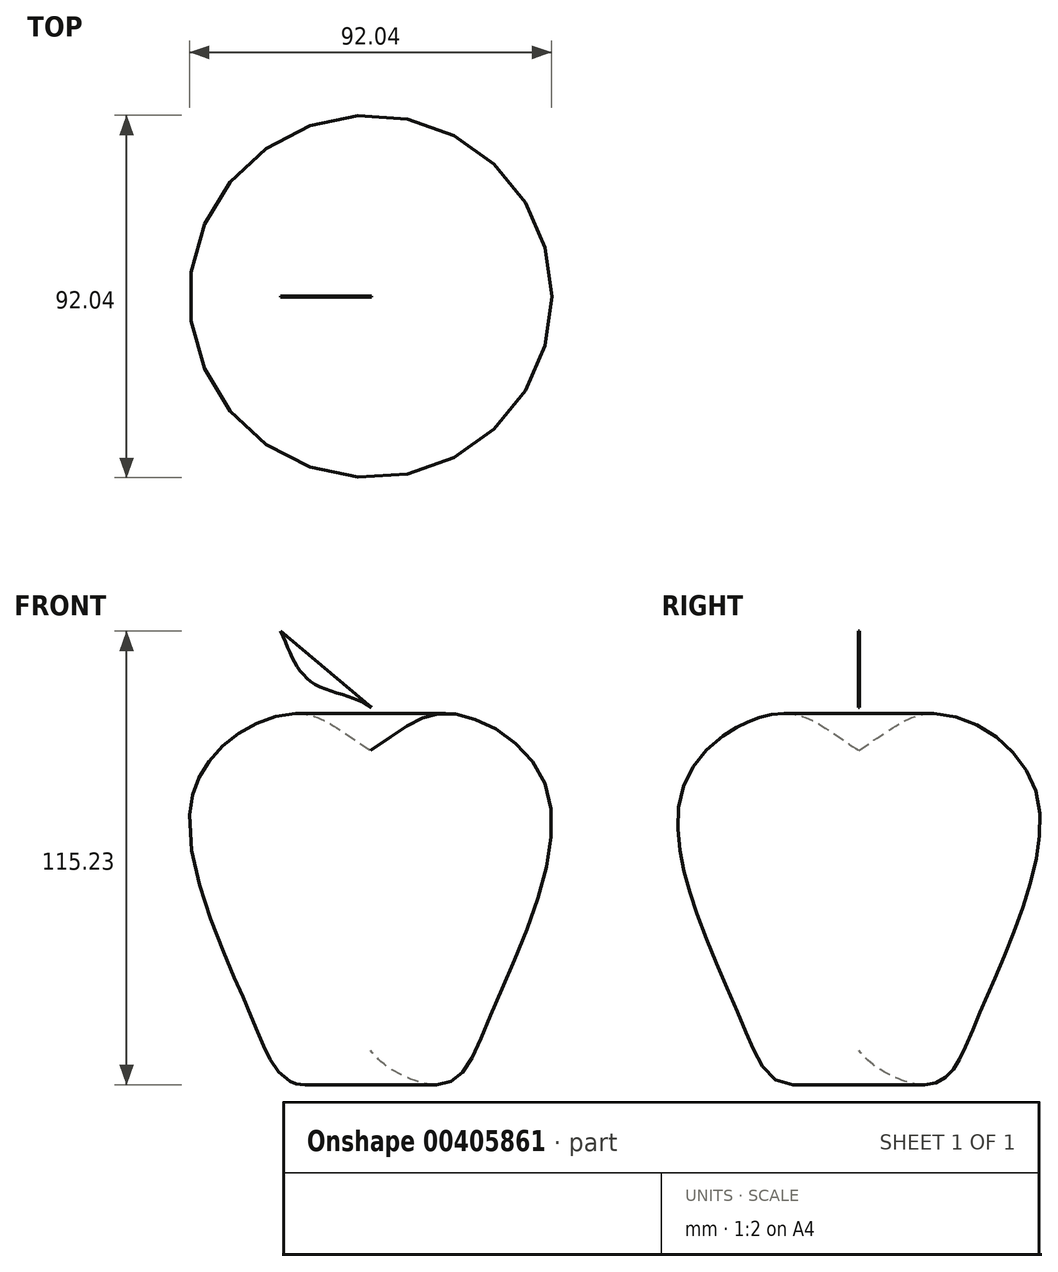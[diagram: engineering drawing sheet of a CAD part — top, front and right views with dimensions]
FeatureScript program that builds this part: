
annotation { "Feature Type Name" : "Feature", "Feature Type Description" : "" }
export const myFeature = defineFeature(function(context is Context, id is Id, definition is map)
    precondition{}
    {
        {
            var Q0;
            Q0=qCreatedBy(makeId("Front.planeOp"),FACE);
            var sketch = newSketch(context, id + "F0", { "sketchPlane" : qUnion([Q0])});
            skLineSegment(sketch, "E0", {"start": v(0, 29.21) * mm, "end": v(0, -46.99) * mm});
            skFitSpline(sketch, "E1", {"points": [v(0, 29.21) * mm, v(20.12, 38.59) * mm, v(44.94, 18.85) * mm, v(30.68, -37.61) * mm, v(18.37, -55.59) * mm, v(0, -46.99) * mm], "startDerivative": vector(151.32, 97.28) * mm, "endDerivative": vector(-65.08, 90.75) * mm});
            skFitSpline(sketch, "E2", {"points": [v(0, 29.21) * mm, v(8.8, 55.78) * mm], "startDerivative": vector(-7.62, 66.82) * mm, "endDerivative": vector(12.9, 5.86) * mm});
            skLineSegment(sketch, "E3", {"start": v(-68.35, 33.7) * mm, "end": v(-38.15, 33.7) * mm});
            skFitSpline(sketch, "E4", {"points": [v(-68.35, 33.7) * mm, v(-52.66, 38.5) * mm, v(-38.15, 33.7) * mm], "startDerivative": vector(26.27, 0) * mm, "endDerivative": vector(32.9, -15.28) * mm});
            skFitSpline(sketch, "E5.MirrorCS", {"points": [v(-68.35, 33.7) * mm, v(-52.66, 28.9) * mm, v(-38.15, 33.7) * mm], "startDerivative": vector(26.27, 0) * mm, "endDerivative": vector(32.9, 15.28) * mm});
            skSolve(sketch);
        }
        {
            var Q0;
            Q0=makeQuery(id+"F0.imprint","IMPRINT",FACE,{"disambiguationData":[TD([[makeQuery(id+"F0.imprint","IMPRINT",EDGE,{"derivedFrom":sQuery(id+"F0.wireOp",EDGE,"E0")}),1.0]])]});
            var Q1;
            Q1=sQuery(id+"F0.wireOp",EDGE,"E0");
            revolve(context, id + "F1", {"entities" : qUnion([Q0]), "axis" : qUnion([Q1]), "revolveType" : RevolveType.FULL});
        }
        {
            var Q0;
            Q0=qCreatedBy(makeId("Top.planeOp"),FACE);
            cPlane(context, id + "F2", {"entities" : qUnion([Q0]), "cplaneType" : CPlaneType.OFFSET, "offset" : 25.4 * mm, "width" : 152.4 * mm, "height" : 152.4 * mm});
        }
        {
            var Q0;
            Q0=qCreatedBy(id+"F2.planeOp",FACE);
            var sketch = newSketch(context, id + "F3", { "sketchPlane" : qUnion([Q0])});
            skCircle(sketch, "E6", {"center": v(0, 0) * mm, "radius": 3.67 * mm});
            skSolve(sketch);
        }
        {
            var Q0;
            Q0=qCreatedBy(makeId("Front.planeOp"),FACE);
            var sketch = newSketch(context, id + "F4", { "sketchPlane" : qUnion([Q0])});
            skFitSpline(sketch, "E7", {"points": [v(0, 25.4) * mm, v(12.46, 51.12) * mm], "startDerivative": vector(-7.62, 66.82) * mm, "endDerivative": vector(19.2, 2.52) * mm});
            skLineSegment(sketch, "E8", {"start": v(0.24, 40.1) * mm, "end": v(-22.9, 59.5) * mm});
            skFitSpline(sketch, "E9", {"points": [v(0.24, 40.1) * mm, v(-14.86, 46.5) * mm, v(-22.9, 59.5) * mm], "startDerivative": vector(-20.13, 16.89) * mm, "endDerivative": vector(-15.39, 32.86) * mm});
            skFitSpline(sketch, "E10.MirrorCS", {"points": [v(0.24, 40.1) * mm, v(-8.7, 53.86) * mm, v(-22.9, 59.5) * mm], "startDerivative": vector(-20.13, 16.89) * mm, "endDerivative": vector(-35.03, 9.45) * mm});
            skSolve(sketch);
        }
        {
            var Q0;
            {var subQ0=sQuery(id+"F4.wireOp",EDGE,"E8");Q0=makeQuery(id+"F4.imprint","IMPRINT",FACE,{"disambiguationData":[TD([[makeQuery(id+"F4.imprint","IMPRINT",EDGE,{"derivedFrom":subQ0}),1.0]])]});}
            var Q1;
            {var subQ0=sQuery(id+"F4.wireOp",EDGE,"E8");Q1=makeQuery(id+"F4.imprint","IMPRINT",FACE,{"disambiguationData":[TD([[makeQuery(id+"F4.imprint","IMPRINT",EDGE,{"derivedFrom":subQ0}),-1.0]])]});}
            extrude(context, id + "F5", {"entities" : qUnion([Q0, Q1]), "endBound" : BoundingType.SYMMETRIC, "depth" : 0.25 * mm});
        }
        {
            var Q0;
            Q0=sQuery(id+"F4.wireOp",EDGE,"E8");
            extrude(context, id + "F6", {"bodyType" : ToolBodyType.SURFACE, "surfaceEntities" : qUnion([Q0]), "endBound" : BoundingType.SYMMETRIC, "depth" : 0.5 * mm});
        }
    });
